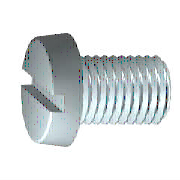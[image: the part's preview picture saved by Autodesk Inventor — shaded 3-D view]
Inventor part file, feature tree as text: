
AUTODESK INVENTOR PART (.ipt)
format: ipt  version: 2023.2 (Build 272271030, 271C)  size: 184,320 bytes
history: native  units: mm (DEFAULTED — no unit token found)
features: sketch x2, extrude x1, plane x1
ambient origin geometry x7: Origin, YZ Plane, XZ Plane, X Axis, Y Axis, Z Axis, Center Point
bodies: Solid1 (feature_tree), Body (feature_tree)
feature tree (4):
  sketch  "Sketch2"  dims[d2=0.49086mm d3=3.3mm d4=5.0mm d5=4.566987mm d8=90.0deg d7=0.0mm d9=8.5mm d10=0.872665mm d11=1.2mm d12=8.5mm d14=0.2mm d15=10.4mm d16=0.0mm d17=0.433015mm d18=0.49086mm d19=1.3mm d20=0.0mm d36=45.0deg d37=0.0mm d39=0.0mm]
  extrude  "Slot"  Depth=10.4mm
  plane  "Work Plane1"
  sketch  "Sketch1"  dims[d0=12.0mm d1=10.4mm]
